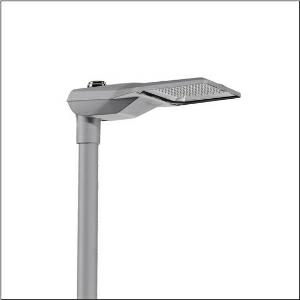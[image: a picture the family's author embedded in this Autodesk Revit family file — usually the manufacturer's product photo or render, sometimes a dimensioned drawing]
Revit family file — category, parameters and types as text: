
# Revit family: streetlight_sl_21_midi___st1_0a_5xe7d37n08mb_3723
name_source: partatom
category: Lighting Fixtures
units: mm (PartAtom-declared; Revit-internal decimal feet)

## family parameters
Cut with Voids When Loaded = No
Host = Face
Light Source = No
Part Type = Normal
Room Calculation Point = No
Round Connector Dimension = Use Diameter
Shared = No

## types (1)
- --- (1 x LED, 18270 lm, 136 W, 3000K)
    Apparent Load = 136 VA
    CIE Flux Codes = 37 72 97 100 100
    Color Rendering = 70
    Color Temperature = 3000K
    Default Elevation = 1800 mm
    Description = Streetlight SL 21 midi, mast luminaire, primary light control with lens, of PMMA, primary optical cover: cover, of toughened safety glass, transparent, light distribution: ST1.0a, light emission: direct distribution, primary light characteristic: asymmetric, installation type: side-entry, LED, 3G 2.5mm², High Power LED, rated luminous flux: 18.270lm, luminous efficacy: 134lm/W, light colour: 730, colour temperature: 3000K, control gear: NEMA (7pin), control: overheat protection, pre-setting: linear dimming characteristic, constant luminous flux control, time-dependent luminous flux control, flexible luminous flux parameterisation, mains connection: 220..240V, AC, 50/60Hz, connection cable pre-assembled, cable length: 12,5m, wiring characteristics: H05VV-F, start of lifetime: 136W, end of service life: 142W, reduction: 61W, luminaire housing, of diecast aluminium (EN AC-44300), powder-coated, Siteco® metallic grey (DB 702S), corrosivity category C5 mid according to DIN EN ISO 12944, multi-level sealing system, sealing non-destructively replaceable, inclination adjustable: 0°, 5°, 10°, 15°, length: 644mm, width: 335mm, height: 110mm, spigot size: 42mm (side-entry), mounting height: 4..8m, protection rating (complete): IP66, insulation class (complete): insulation class I (protective earthing), certification: CE, ENEC, ENEC+, VDE, impact resistance: IK10, permissible operating ambient temperature for outdoor applications: -40..+50°C, standard-compliant lighting for roads and squares, packaging unit: 1 piece

Light Distribution: ST1.0a
    Height = 111 mm
    Lamp = 1 x LED
    Lamp Light Flux = 18270 lm
    Lamp Power = 136 W
    Lamp count = 1
    Length = 644 mm
    Luminous efficacy = 134 lm/W
    Manufacturer = Siteco
    ModVariant = No
    Model = 5XE7D37N08MB
    Number of Poles = 1
    OnlyDefault = Yes
    Power Factor = 1
    Product Name = Streetlight SL 21 midi | ST1.0a
    Product group = mast luminaire | pylon top
    ProductGroupID = 6100
    Protection Class = Protection class I
    Protection Degree = IP 66
    RLX_Detail_Level = 1
    RLX_Emergency_Light_Flux = 0 lm
    RLX_Emergency_Type = 0
    RLX_Emergency_Type_DB = No
    RlxData = <blob elided: 26453 chars, md5=76a4da9e>
    Socket = socket
    Standby Power = 0 W
    System Light Flux = 18270 lm
    System Power = 136 W
    Type Comments = factory setting: luminous flux: 100 % | dim-lin: 254 | 695 mA
    Type Image = l_1294377.jpg
    URL = http://relux.com
    VarID = @adj_136048
    Voltage = 0 V
    Weight = 0.00 kg
    Width = 336 mm

## geometry (parser evidence)
native form markers: Blend x4, Sweep x12
no freeform markers — native parametric forms only
